# Revit family: C8269
name_source: partatom
category: Specialty Equipment
units: mm (PartAtom-declared; Revit-internal decimal feet)

## family parameters
Always vertical = Yes
Cut with Voids When Loaded = No
Maintain Annotation Orientation = No
Part Type = Normal
Room Calculation Point = No
Round Connector Dimension = Use Diameter
Shared = No
Work Plane-Based = No

## types (1)
- C8269 Hose Reel
    Cold Water Consumption = 3 GPM
    Cold Water Flow Rate = 3 GPM
    Cold Water Inlet Flow = 3 GPM
    Cold Water Maximum Pressure = 125.00 psi
    Cold Water Minimum Pressure = 20.00 psi
    Cold Water Size = 0' - 0 3/8"
    Cold water Temerature Recommended = 40 °F
    Connector 1 Description = Hot Water Inlet
    Connector 2 Description = Cold Water Inlet
    Default Elevation = 0' - 0"
    Description = Hose Reel
    Hot Water Consumption = 3 GPM
    Hot Water Flow Rate = 3 GPM
    Hot Water Inlet Flow = 3 GPM
    Hot Water Maximum Pressure = 125.00 psi
    Hot Water Minimum Pressure = 20.00 psi
    Hot Water Size = 0' - 0 3/8"
    Hot water Temerature = 140 °F
    Manufacturer = Krome Usa Inc.
    Material = Coated Steel
    Maximum Temperature = 140 °F
    Minimum Teperature = 40 °F
    Model = C8269
    Product Name = Epoxy Coated Water Hose Reel 16 Miter (3/8"X52 FT)
    URL = https://www.aluids.com
    Water Supply Radius = 0' - 0 3/16"

## geometry (parser evidence)
native form markers: Sweep x2
no freeform markers — native parametric forms only
